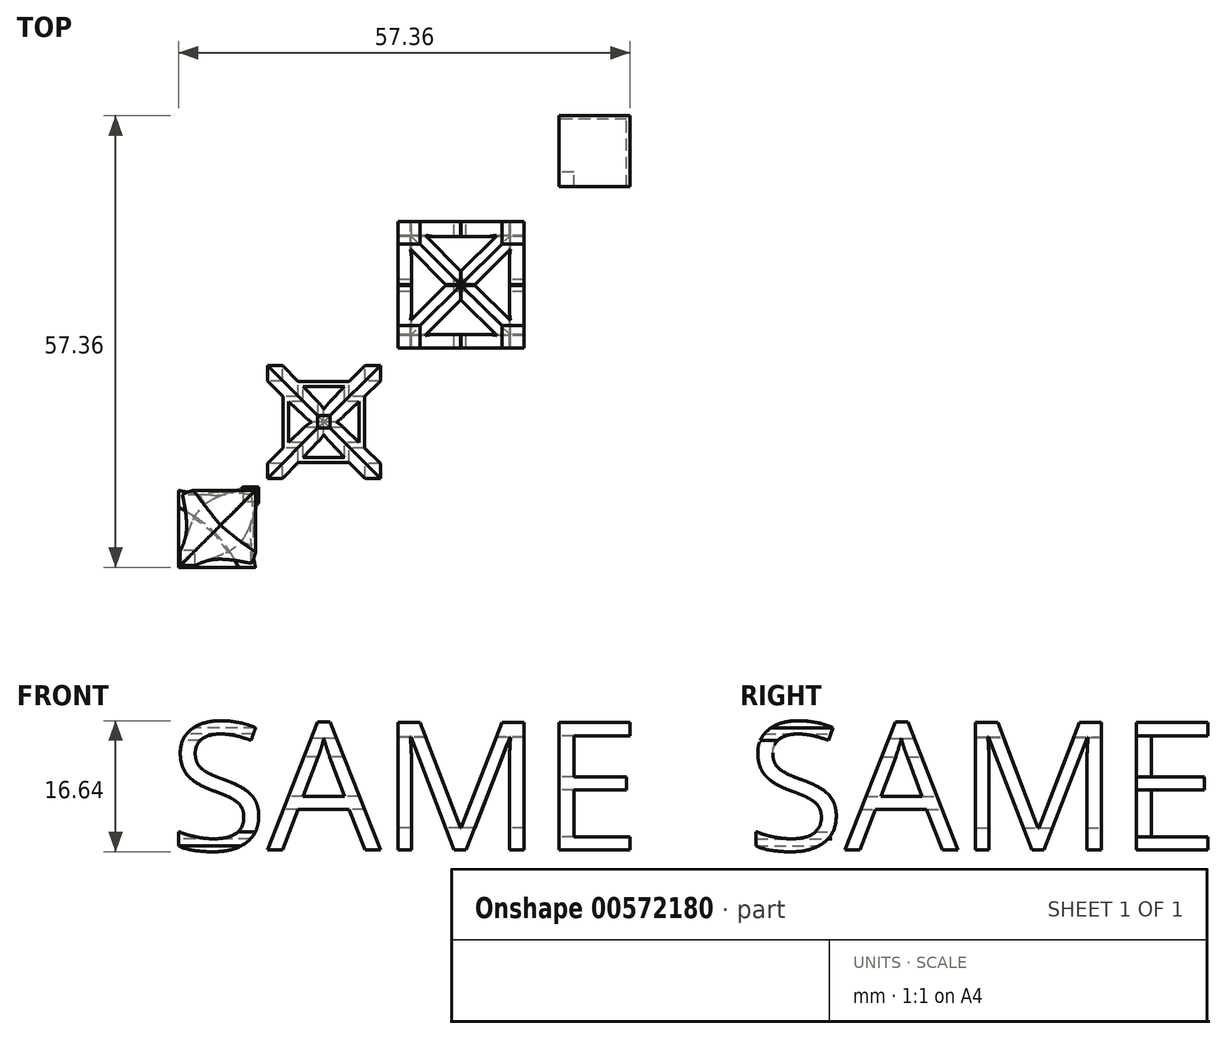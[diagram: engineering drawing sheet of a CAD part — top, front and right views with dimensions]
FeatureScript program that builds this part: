
annotation { "Feature Type Name" : "Feature", "Feature Type Description" : "" }
export const myFeature = defineFeature(function(context is Context, id is Id, definition is map)
    precondition{}
    {
        {
            var Q0;
            Q0=qCreatedBy(makeId("Front.planeOp"),FACE);
            var sketch = newSketch(context, id + "F0", { "sketchPlane" : qUnion([Q0])});
            skText(sketch, "E0", { "text": "SAME", "fontName": "OpenSans-Regular.ttf"});
            const initialGuessF0  = {"E0": [0, 0, 1, 0, 0.01633]};
            skSetInitialGuess(sketch, initialGuessF0);
            skSolve(sketch);
        }
        {
            var Q0;
            Q0=qCreatedBy(makeId("Right.planeOp"),FACE);
            var sketch = newSketch(context, id + "F1", { "sketchPlane" : qUnion([Q0])});
            skText(sketch, "E1", { "text": "SAME", "fontName": "OpenSans-Regular.ttf"});
            const initialGuessF1  = {"E1": [-0.06, 0, 1, 0, 0.01633]};
            skSetInitialGuess(sketch, initialGuessF1);
            skSolve(sketch);
        }
        {
            var Q0;
            Q0=makeQuery(id+"F0.imprint","IMPRINT",FACE,{"disambiguationData":[TD([[makeQuery(id+"F0.imprint","IMPRINT",EDGE,{"derivedFrom":sQuery(id+"F0.wireOp",EDGE,"E0.sketch_text.stroke-0")}),-1.0]])]});
            var Q1;
            Q1=makeQuery(id+"F0.imprint","IMPRINT",FACE,{"disambiguationData":[TD([[makeQuery(id+"F0.imprint","IMPRINT",EDGE,{"derivedFrom":sQuery(id+"F0.wireOp",EDGE,"E0.sketch_text.stroke-25")}),-1.0]])]});
            var Q2;
            Q2=makeQuery(id+"F0.imprint","IMPRINT",FACE,{"disambiguationData":[TD([[makeQuery(id+"F0.imprint","IMPRINT",EDGE,{"derivedFrom":sQuery(id+"F0.wireOp",EDGE,"E0.sketch_text.stroke-38")}),-1.0]])]});
            var Q3;
            Q3=makeQuery(id+"F0.imprint","IMPRINT",FACE,{"disambiguationData":[TD([[makeQuery(id+"F0.imprint","IMPRINT",EDGE,{"derivedFrom":sQuery(id+"F0.wireOp",EDGE,"E0.sketch_text.stroke-56")}),-1.0]])]});
            extrude(context, id + "F2", {"entities" : qUnion([Q0, Q1, Q2, Q3]), "depth" : 60 * mm, "offsetDistance" : 25 * mm});
        }
        {
            var Q0;
            Q0=makeQuery(id+"F1.imprint","IMPRINT",FACE,{"disambiguationData":[TD([[makeQuery(id+"F1.imprint","IMPRINT",EDGE,{"derivedFrom":sQuery(id+"F1.wireOp",EDGE,"E1.sketch_text.stroke-0")}),-1.0]])]});
            var Q1;
            Q1=makeQuery(id+"F1.imprint","IMPRINT",FACE,{"disambiguationData":[TD([[makeQuery(id+"F1.imprint","IMPRINT",EDGE,{"derivedFrom":sQuery(id+"F1.wireOp",EDGE,"E1.sketch_text.stroke-25")}),-1.0]])]});
            var Q2;
            Q2=makeQuery(id+"F1.imprint","IMPRINT",FACE,{"disambiguationData":[TD([[makeQuery(id+"F1.imprint","IMPRINT",EDGE,{"derivedFrom":sQuery(id+"F1.wireOp",EDGE,"E1.sketch_text.stroke-38")}),-1.0]])]});
            var Q3;
            Q3=makeQuery(id+"F1.imprint","IMPRINT",FACE,{"disambiguationData":[TD([[makeQuery(id+"F1.imprint","IMPRINT",EDGE,{"derivedFrom":sQuery(id+"F1.wireOp",EDGE,"E1.sketch_text.stroke-56")}),-1.0]])]});
            extrude(context, id + "F3", {"entities" : qUnion([Q0, Q1, Q2, Q3]), "depth" : 65 * mm, "offsetDistance" : 25 * mm});
        }
        {
            var Q0;
            Q0=makeQuery(id+"F3.opExtrude","SWEPT_BODY",BODY,{"disambiguationData":[OSD([sQuery(id+"F1.wireOp",EDGE,"E1.sketch_text.stroke-0"),sQuery(id+"F1.wireOp",EDGE,"E1.sketch_text.stroke-1"),sQuery(id+"F1.wireOp",EDGE,"E1.sketch_text.stroke-2"),sQuery(id+"F1.wireOp",EDGE,"E1.sketch_text.stroke-3"),sQuery(id+"F1.wireOp",EDGE,"E1.sketch_text.stroke-4"),sQuery(id+"F1.wireOp",EDGE,"E1.sketch_text.stroke-5"),sQuery(id+"F1.wireOp",EDGE,"E1.sketch_text.stroke-6"),sQuery(id+"F1.wireOp",EDGE,"E1.sketch_text.stroke-7"),sQuery(id+"F1.wireOp",EDGE,"E1.sketch_text.stroke-8"),sQuery(id+"F1.wireOp",EDGE,"E1.sketch_text.stroke-9"),sQuery(id+"F1.wireOp",EDGE,"E1.sketch_text.stroke-10"),sQuery(id+"F1.wireOp",EDGE,"E1.sketch_text.stroke-11"),sQuery(id+"F1.wireOp",EDGE,"E1.sketch_text.stroke-12"),sQuery(id+"F1.wireOp",EDGE,"E1.sketch_text.stroke-13"),sQuery(id+"F1.wireOp",EDGE,"E1.sketch_text.stroke-14"),sQuery(id+"F1.wireOp",EDGE,"E1.sketch_text.stroke-15"),sQuery(id+"F1.wireOp",EDGE,"E1.sketch_text.stroke-16"),sQuery(id+"F1.wireOp",EDGE,"E1.sketch_text.stroke-17"),sQuery(id+"F1.wireOp",EDGE,"E1.sketch_text.stroke-18"),sQuery(id+"F1.wireOp",EDGE,"E1.sketch_text.stroke-19"),sQuery(id+"F1.wireOp",EDGE,"E1.sketch_text.stroke-20"),sQuery(id+"F1.wireOp",EDGE,"E1.sketch_text.stroke-21"),sQuery(id+"F1.wireOp",EDGE,"E1.sketch_text.stroke-22"),sQuery(id+"F1.wireOp",EDGE,"E1.sketch_text.stroke-23"),sQuery(id+"F1.wireOp",EDGE,"E1.sketch_text.stroke-24")])]});
            var Q1;
            Q1=makeQuery(id+"F2.opExtrude","SWEPT_BODY",BODY,{"disambiguationData":[OSD([sQuery(id+"F0.wireOp",EDGE,"E0.sketch_text.stroke-0"),sQuery(id+"F0.wireOp",EDGE,"E0.sketch_text.stroke-1"),sQuery(id+"F0.wireOp",EDGE,"E0.sketch_text.stroke-2"),sQuery(id+"F0.wireOp",EDGE,"E0.sketch_text.stroke-3"),sQuery(id+"F0.wireOp",EDGE,"E0.sketch_text.stroke-4"),sQuery(id+"F0.wireOp",EDGE,"E0.sketch_text.stroke-5"),sQuery(id+"F0.wireOp",EDGE,"E0.sketch_text.stroke-6"),sQuery(id+"F0.wireOp",EDGE,"E0.sketch_text.stroke-7"),sQuery(id+"F0.wireOp",EDGE,"E0.sketch_text.stroke-8"),sQuery(id+"F0.wireOp",EDGE,"E0.sketch_text.stroke-9"),sQuery(id+"F0.wireOp",EDGE,"E0.sketch_text.stroke-10"),sQuery(id+"F0.wireOp",EDGE,"E0.sketch_text.stroke-11"),sQuery(id+"F0.wireOp",EDGE,"E0.sketch_text.stroke-12"),sQuery(id+"F0.wireOp",EDGE,"E0.sketch_text.stroke-13"),sQuery(id+"F0.wireOp",EDGE,"E0.sketch_text.stroke-14"),sQuery(id+"F0.wireOp",EDGE,"E0.sketch_text.stroke-15"),sQuery(id+"F0.wireOp",EDGE,"E0.sketch_text.stroke-16"),sQuery(id+"F0.wireOp",EDGE,"E0.sketch_text.stroke-17"),sQuery(id+"F0.wireOp",EDGE,"E0.sketch_text.stroke-18"),sQuery(id+"F0.wireOp",EDGE,"E0.sketch_text.stroke-19"),sQuery(id+"F0.wireOp",EDGE,"E0.sketch_text.stroke-20"),sQuery(id+"F0.wireOp",EDGE,"E0.sketch_text.stroke-21"),sQuery(id+"F0.wireOp",EDGE,"E0.sketch_text.stroke-22"),sQuery(id+"F0.wireOp",EDGE,"E0.sketch_text.stroke-23"),sQuery(id+"F0.wireOp",EDGE,"E0.sketch_text.stroke-24")])]});
            booleanBodies(context, id + "F4", {"operationType" : BooleanOperationType.INTERSECTION, "tools" : qUnion([Q0, Q1])});
        }
        {
            var Q0;
            Q0=makeQuery(id+"F3.opExtrude","SWEPT_BODY",BODY,{"disambiguationData":[OSD([sQuery(id+"F1.wireOp",EDGE,"E1.sketch_text.stroke-25"),sQuery(id+"F1.wireOp",EDGE,"E1.sketch_text.stroke-26"),sQuery(id+"F1.wireOp",EDGE,"E1.sketch_text.stroke-27"),sQuery(id+"F1.wireOp",EDGE,"E1.sketch_text.stroke-28"),sQuery(id+"F1.wireOp",EDGE,"E1.sketch_text.stroke-29"),sQuery(id+"F1.wireOp",EDGE,"E1.sketch_text.stroke-30"),sQuery(id+"F1.wireOp",EDGE,"E1.sketch_text.stroke-31"),sQuery(id+"F1.wireOp",EDGE,"E1.sketch_text.stroke-32"),sQuery(id+"F1.wireOp",EDGE,"E1.sketch_text.stroke-33"),sQuery(id+"F1.wireOp",EDGE,"E1.sketch_text.stroke-34"),sQuery(id+"F1.wireOp",EDGE,"E1.sketch_text.stroke-35"),sQuery(id+"F1.wireOp",EDGE,"E1.sketch_text.stroke-36"),sQuery(id+"F1.wireOp",EDGE,"E1.sketch_text.stroke-37")])]});
            var Q1;
            Q1=makeQuery(id+"F2.opExtrude","SWEPT_BODY",BODY,{"disambiguationData":[OSD([sQuery(id+"F0.wireOp",EDGE,"E0.sketch_text.stroke-25"),sQuery(id+"F0.wireOp",EDGE,"E0.sketch_text.stroke-26"),sQuery(id+"F0.wireOp",EDGE,"E0.sketch_text.stroke-27"),sQuery(id+"F0.wireOp",EDGE,"E0.sketch_text.stroke-28"),sQuery(id+"F0.wireOp",EDGE,"E0.sketch_text.stroke-29"),sQuery(id+"F0.wireOp",EDGE,"E0.sketch_text.stroke-30"),sQuery(id+"F0.wireOp",EDGE,"E0.sketch_text.stroke-31"),sQuery(id+"F0.wireOp",EDGE,"E0.sketch_text.stroke-32"),sQuery(id+"F0.wireOp",EDGE,"E0.sketch_text.stroke-33"),sQuery(id+"F0.wireOp",EDGE,"E0.sketch_text.stroke-34"),sQuery(id+"F0.wireOp",EDGE,"E0.sketch_text.stroke-35"),sQuery(id+"F0.wireOp",EDGE,"E0.sketch_text.stroke-36"),sQuery(id+"F0.wireOp",EDGE,"E0.sketch_text.stroke-37")])]});
            var Q2;
            Q2=makeQuery(id+"F2.opExtrude","SWEPT_BODY",BODY,{"disambiguationData":[OSD([sQuery(id+"F0.wireOp",EDGE,"E0.sketch_text.stroke-25"),sQuery(id+"F0.wireOp",EDGE,"E0.sketch_text.stroke-26"),sQuery(id+"F0.wireOp",EDGE,"E0.sketch_text.stroke-27"),sQuery(id+"F0.wireOp",EDGE,"E0.sketch_text.stroke-28"),sQuery(id+"F0.wireOp",EDGE,"E0.sketch_text.stroke-29"),sQuery(id+"F0.wireOp",EDGE,"E0.sketch_text.stroke-30"),sQuery(id+"F0.wireOp",EDGE,"E0.sketch_text.stroke-31"),sQuery(id+"F0.wireOp",EDGE,"E0.sketch_text.stroke-32"),sQuery(id+"F0.wireOp",EDGE,"E0.sketch_text.stroke-33"),sQuery(id+"F0.wireOp",EDGE,"E0.sketch_text.stroke-34"),sQuery(id+"F0.wireOp",EDGE,"E0.sketch_text.stroke-35"),sQuery(id+"F0.wireOp",EDGE,"E0.sketch_text.stroke-36"),sQuery(id+"F0.wireOp",EDGE,"E0.sketch_text.stroke-37")])]});
            booleanBodies(context, id + "F5", {"operationType" : BooleanOperationType.INTERSECTION, "tools" : qUnion([Q0, Q1]), "targets" : qUnion([Q2])});
        }
        {
            var Q0;
            Q0=makeQuery(id+"F2.opExtrude","SWEPT_BODY",BODY,{"disambiguationData":[OSD([sQuery(id+"F0.wireOp",EDGE,"E0.sketch_text.stroke-38"),sQuery(id+"F0.wireOp",EDGE,"E0.sketch_text.stroke-39"),sQuery(id+"F0.wireOp",EDGE,"E0.sketch_text.stroke-40"),sQuery(id+"F0.wireOp",EDGE,"E0.sketch_text.stroke-41"),sQuery(id+"F0.wireOp",EDGE,"E0.sketch_text.stroke-42"),sQuery(id+"F0.wireOp",EDGE,"E0.sketch_text.stroke-43"),sQuery(id+"F0.wireOp",EDGE,"E0.sketch_text.stroke-44"),sQuery(id+"F0.wireOp",EDGE,"E0.sketch_text.stroke-45"),sQuery(id+"F0.wireOp",EDGE,"E0.sketch_text.stroke-46"),sQuery(id+"F0.wireOp",EDGE,"E0.sketch_text.stroke-47"),sQuery(id+"F0.wireOp",EDGE,"E0.sketch_text.stroke-48"),sQuery(id+"F0.wireOp",EDGE,"E0.sketch_text.stroke-49"),sQuery(id+"F0.wireOp",EDGE,"E0.sketch_text.stroke-50"),sQuery(id+"F0.wireOp",EDGE,"E0.sketch_text.stroke-51"),sQuery(id+"F0.wireOp",EDGE,"E0.sketch_text.stroke-52"),sQuery(id+"F0.wireOp",EDGE,"E0.sketch_text.stroke-53"),sQuery(id+"F0.wireOp",EDGE,"E0.sketch_text.stroke-54"),sQuery(id+"F0.wireOp",EDGE,"E0.sketch_text.stroke-55")])]});
            var Q1;
            Q1=makeQuery(id+"F3.opExtrude","SWEPT_BODY",BODY,{"disambiguationData":[OSD([sQuery(id+"F1.wireOp",EDGE,"E1.sketch_text.stroke-38"),sQuery(id+"F1.wireOp",EDGE,"E1.sketch_text.stroke-39"),sQuery(id+"F1.wireOp",EDGE,"E1.sketch_text.stroke-40"),sQuery(id+"F1.wireOp",EDGE,"E1.sketch_text.stroke-41"),sQuery(id+"F1.wireOp",EDGE,"E1.sketch_text.stroke-42"),sQuery(id+"F1.wireOp",EDGE,"E1.sketch_text.stroke-43"),sQuery(id+"F1.wireOp",EDGE,"E1.sketch_text.stroke-44"),sQuery(id+"F1.wireOp",EDGE,"E1.sketch_text.stroke-45"),sQuery(id+"F1.wireOp",EDGE,"E1.sketch_text.stroke-46"),sQuery(id+"F1.wireOp",EDGE,"E1.sketch_text.stroke-47"),sQuery(id+"F1.wireOp",EDGE,"E1.sketch_text.stroke-48"),sQuery(id+"F1.wireOp",EDGE,"E1.sketch_text.stroke-49"),sQuery(id+"F1.wireOp",EDGE,"E1.sketch_text.stroke-50"),sQuery(id+"F1.wireOp",EDGE,"E1.sketch_text.stroke-51"),sQuery(id+"F1.wireOp",EDGE,"E1.sketch_text.stroke-52"),sQuery(id+"F1.wireOp",EDGE,"E1.sketch_text.stroke-53"),sQuery(id+"F1.wireOp",EDGE,"E1.sketch_text.stroke-54"),sQuery(id+"F1.wireOp",EDGE,"E1.sketch_text.stroke-55")])]});
            booleanBodies(context, id + "F6", {"operationType" : BooleanOperationType.INTERSECTION, "tools" : qUnion([Q0, Q1])});
        }
        {
            var Q0;
            Q0=makeQuery(id+"F2.opExtrude","SWEPT_BODY",BODY,{"disambiguationData":[OSD([sQuery(id+"F0.wireOp",EDGE,"E0.sketch_text.stroke-56"),sQuery(id+"F0.wireOp",EDGE,"E0.sketch_text.stroke-57"),sQuery(id+"F0.wireOp",EDGE,"E0.sketch_text.stroke-58"),sQuery(id+"F0.wireOp",EDGE,"E0.sketch_text.stroke-59"),sQuery(id+"F0.wireOp",EDGE,"E0.sketch_text.stroke-60"),sQuery(id+"F0.wireOp",EDGE,"E0.sketch_text.stroke-61"),sQuery(id+"F0.wireOp",EDGE,"E0.sketch_text.stroke-62"),sQuery(id+"F0.wireOp",EDGE,"E0.sketch_text.stroke-63"),sQuery(id+"F0.wireOp",EDGE,"E0.sketch_text.stroke-64"),sQuery(id+"F0.wireOp",EDGE,"E0.sketch_text.stroke-65"),sQuery(id+"F0.wireOp",EDGE,"E0.sketch_text.stroke-66"),sQuery(id+"F0.wireOp",EDGE,"E0.sketch_text.stroke-67")])]});
            var Q1;
            Q1=makeQuery(id+"F3.opExtrude","SWEPT_BODY",BODY,{"disambiguationData":[OSD([sQuery(id+"F1.wireOp",EDGE,"E1.sketch_text.stroke-56"),sQuery(id+"F1.wireOp",EDGE,"E1.sketch_text.stroke-57"),sQuery(id+"F1.wireOp",EDGE,"E1.sketch_text.stroke-58"),sQuery(id+"F1.wireOp",EDGE,"E1.sketch_text.stroke-59"),sQuery(id+"F1.wireOp",EDGE,"E1.sketch_text.stroke-60"),sQuery(id+"F1.wireOp",EDGE,"E1.sketch_text.stroke-61"),sQuery(id+"F1.wireOp",EDGE,"E1.sketch_text.stroke-62"),sQuery(id+"F1.wireOp",EDGE,"E1.sketch_text.stroke-63"),sQuery(id+"F1.wireOp",EDGE,"E1.sketch_text.stroke-64"),sQuery(id+"F1.wireOp",EDGE,"E1.sketch_text.stroke-65"),sQuery(id+"F1.wireOp",EDGE,"E1.sketch_text.stroke-66"),sQuery(id+"F1.wireOp",EDGE,"E1.sketch_text.stroke-67")])]});
            booleanBodies(context, id + "F7", {"operationType" : BooleanOperationType.INTERSECTION, "tools" : qUnion([Q0, Q1])});
        }
    });
